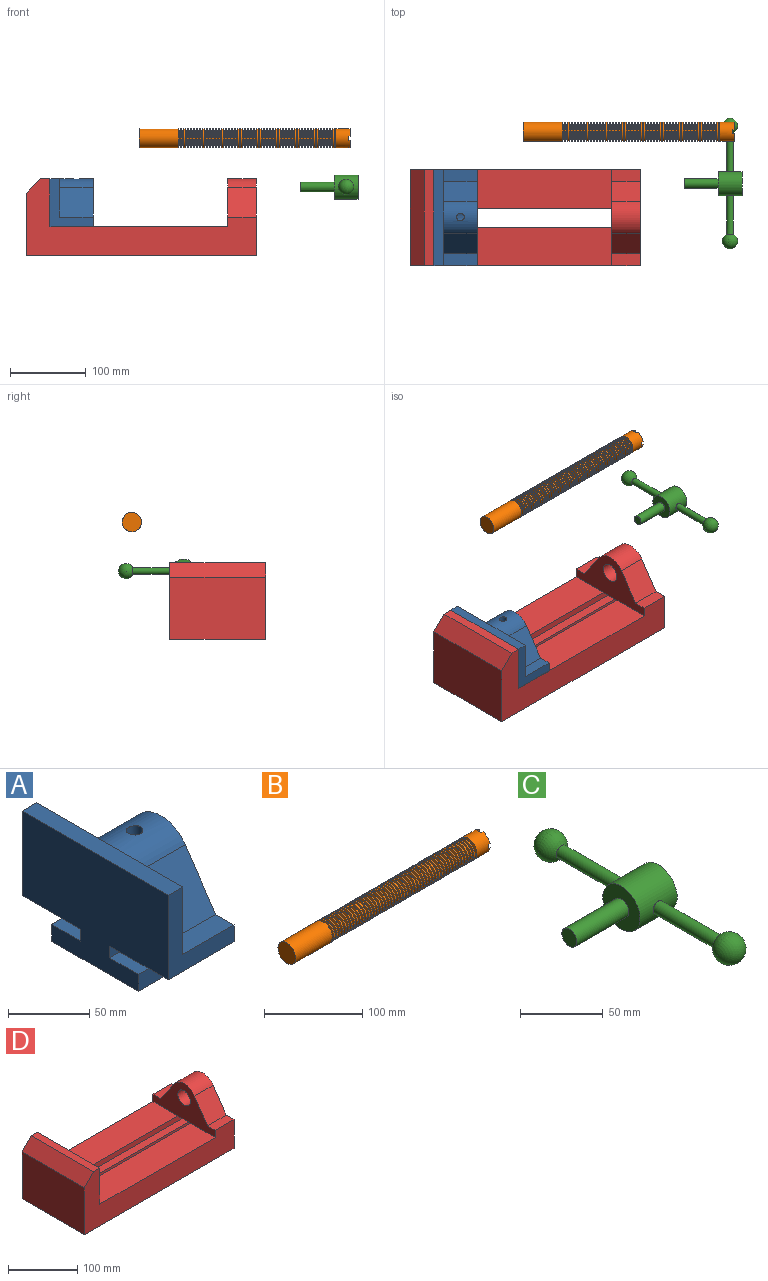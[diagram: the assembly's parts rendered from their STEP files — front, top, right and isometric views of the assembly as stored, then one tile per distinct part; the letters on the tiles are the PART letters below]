
ASSEMBLY  parts=4 mates=1
PART A: 23 faces, bbox 57.2x127x85.1 mm
  f0: plane 57.15x50.8mm, normal (0,0,-1), area 2903.2mm2, adj f3,f7,f8,f16
  f1: plane 44.45x15.91mm, normal (0,0,1), area 707.2mm2, adj f3,f5,f9,f11
  f2: plane 57.15x50.8mm, normal (0,0,-1), area 2903.2mm2, adj f3,f7,f9,f22
  f3: plane 127x84.76mm, normal (1,0,0), area 5318.8mm2, adj f0,f1,f2,f4,f8,f9,f10,f11
  f4: plane 44.45x15.84mm, normal (0,0,1), area 704mm2, adj f3,f5,f8,f10
  f5: plane 127x50.8mm, normal (1,0,0), area 3422.8mm2, adj f1,f4,f6,f8,f9,f10,f11,f13
  f6: plane 127x12.7mm, normal (0,0,1), area 1612.9mm2, adj f5,f7,f8,f9
  f7: plane 127x85.09mm, normal (-1,0,0), area 9248.3mm2, adj f0,f2,f6,f8,f9,f16,f17,f18
  f8: plane 63.5x57.15mm, normal (0,-1,0), area 1371mm2, adj f0,f3,f4,f5,f6,f7
  f9: plane 63.5x57.15mm, normal (0,1,0), area 1371mm2, adj f1,f2,f3,f5,f6,f7
  f10: plane 44.45x39.31mm, normal (0,-0.83,0.56), area 2110mm2, adj f3,f4,f5,f13
  f11: plane 44.45x39.29mm, normal (0,0.83,0.56), area 2108.2mm2, adj f1,f3,f5,f13
  f12: cylinder r=12.7mm len=44.45mm, axis (1,0,0), area 3463.8mm2, adj f3,f14,f15
  f13: cylinder r=25.4mm len=44.45mm, axis (1,0,0), area 2122.5mm2, adj f3,f5,f10,f11,f15
  f14: plane 25.4x25.4mm, normal (1,0,0), area 506.7mm2, adj f12
  f15: cylinder r=5.08mm len=13.76mm, axis (0,0,1), area 403.7mm2, adj f12,f13
  f16: plane 57.15x8.89mm, normal (0,-1,0), area 508.1mm2, adj f0,f3,f7,f17
  f17: plane 57.15x25.02mm, normal (0,0,1), area 1429.6mm2, adj f3,f7,f16,f18
  f18: plane 57.15x12.7mm, normal (0,-1,0), area 725.8mm2, adj f3,f7,f17,f19
  f19: plane 75.43x57.15mm, normal (0,0,-1), area 4310.9mm2, adj f3,f7,f18,f20
  f20: plane 57.15x12.7mm, normal (0,1,0), area 725.8mm2, adj f3,f7,f19,f21
  f21: plane 57.15x25.02mm, normal (0,0,1), area 1429.6mm2, adj f3,f7,f20,f22
  f22: plane 57.15x8.89mm, normal (0,1,0), area 508.1mm2, adj f2,f3,f7,f21
PART B: 220 faces, bbox 279.4x25.4x25.4 mm
  f0: cylinder r=12.7mm len=25.4mm, axis (-1,0,0), area 1468.2mm2, adj f1,f2,f3,f4,f7,f208,f209,f210
  f1: plane 9.9x9.9mm, normal (1,0,0), area 62.3mm2, adj f0,f5,f215,f217
  f2: plane 9.9x9.9mm, normal (1,0,0), area 62.3mm2, adj f0,f5,f209,f218
  f3: plane 9.9x9.9mm, normal (1,0,0), area 62.3mm2, adj f0,f5,f211,f214
  f4: plane 9.9x9.9mm, normal (1,0,0), area 62.3mm2, adj f0,f5,f208,f212
  f5: cylinder r=6.35mm len=25.4mm, axis (1,0,0), area 960.3mm2, adj f1,f2,f3,f4,f6,f208,f209,f210
  f6: plane 12.7x12.7mm, normal (1,0,0), area 126.7mm2, adj f5
  f7: cone r=12.7mm half-angle=76deg, axis (1,0,0), area 188mm2, adj f0,f9
  f8: cone r=12.7mm half-angle=76deg, axis (-1,0,0), area 188mm2, adj f9,f10
  f9: cylinder r=10.16mm len=20.32mm, axis (1,0,0), area 81.1mm2, adj f7,f8
  f10: cylinder r=12.7mm len=25.4mm, axis (-1,0,0), area 131.7mm2, adj f8,f11
  f11: cone r=12.7mm half-angle=76deg, axis (1,0,0), area 188mm2, adj f10,f13
  f12: cone r=12.7mm half-angle=76deg, axis (-1,0,0), area 188mm2, adj f13,f14
  f13: cylinder r=10.16mm len=20.32mm, axis (1,0,0), area 81.1mm2, adj f11,f12
  f14: cylinder r=12.7mm len=25.4mm, axis (-1,0,0), area 131.7mm2, adj f12,f15
  f15: cone r=12.7mm half-angle=76deg, axis (1,0,0), area 188mm2, adj f14,f17
  f16: cone r=12.7mm half-angle=76deg, axis (-1,0,0), area 188mm2, adj f17,f18
  f17: cylinder r=10.16mm len=20.32mm, axis (1,0,0), area 81.1mm2, adj f15,f16
  f18: cylinder r=12.7mm len=25.4mm, axis (-1,0,0), area 131.7mm2, adj f16,f19
  f19: cone r=12.7mm half-angle=76deg, axis (1,0,0), area 188mm2, adj f18,f21
  f20: cone r=12.7mm half-angle=76deg, axis (-1,0,0), area 188mm2, adj f21,f22
  f21: cylinder r=10.16mm len=20.32mm, axis (1,0,0), area 81.1mm2, adj f19,f20
  f22: cylinder r=12.7mm len=25.4mm, axis (-1,0,0), area 131.7mm2, adj f20,f23
  f23: cone r=12.7mm half-angle=76deg, axis (1,0,0), area 188mm2, adj f22,f25
  f24: cone r=12.7mm half-angle=76deg, axis (-1,0,0), area 188mm2, adj f25,f26
  f25: cylinder r=10.16mm len=20.32mm, axis (1,0,0), area 81.1mm2, adj f23,f24
  f26: cylinder r=12.7mm len=25.4mm, axis (-1,0,0), area 131.7mm2, adj f24,f27
  f27: cone r=12.7mm half-angle=76deg, axis (1,0,0), area 188mm2, adj f26,f29
  f28: cone r=12.7mm half-angle=76deg, axis (-1,0,0), area 188mm2, adj f29,f30
  f29: cylinder r=10.16mm len=20.32mm, axis (1,0,0), area 81.1mm2, adj f27,f28
  f30: cylinder r=12.7mm len=25.4mm, axis (-1,0,0), area 131.7mm2, adj f28,f31
  f31: cone r=12.7mm half-angle=76deg, axis (1,0,0), area 188mm2, adj f30,f33
  f32: cone r=12.7mm half-angle=76deg, axis (-1,0,0), area 188mm2, adj f33,f34
  f33: cylinder r=10.16mm len=20.32mm, axis (1,0,0), area 81.1mm2, adj f31,f32
  f34: cylinder r=12.7mm len=25.4mm, axis (-1,0,0), area 131.7mm2, adj f32,f35
  f35: cone r=12.7mm half-angle=76deg, axis (1,0,0), area 188mm2, adj f34,f37
  f36: cone r=12.7mm half-angle=76deg, axis (-1,0,0), area 188mm2, adj f37,f38
  f37: cylinder r=10.16mm len=20.32mm, axis (1,0,0), area 81.1mm2, adj f35,f36
  f38: cylinder r=12.7mm len=25.4mm, axis (-1,0,0), area 131.7mm2, adj f36,f39
  f39: cone r=12.7mm half-angle=76deg, axis (1,0,0), area 188mm2, adj f38,f41
  f40: cone r=12.7mm half-angle=76deg, axis (-1,0,0), area 188mm2, adj f41,f42
  f41: cylinder r=10.16mm len=20.32mm, axis (1,0,0), area 81.1mm2, adj f39,f40
  f42: cylinder r=12.7mm len=25.4mm, axis (-1,0,0), area 131.7mm2, adj f40,f43
  f43: cone r=12.7mm half-angle=76deg, axis (1,0,0), area 188mm2, adj f42,f45
  f44: cone r=12.7mm half-angle=76deg, axis (-1,0,0), area 188mm2, adj f45,f46
  f45: cylinder r=10.16mm len=20.32mm, axis (1,0,0), area 81.1mm2, adj f43,f44
  f46: cylinder r=12.7mm len=25.4mm, axis (-1,0,0), area 131.7mm2, adj f44,f47
  f47: cone r=12.7mm half-angle=76deg, axis (1,0,0), area 188mm2, adj f46,f49
  f48: cone r=12.7mm half-angle=76deg, axis (-1,0,0), area 188mm2, adj f49,f50
  f49: cylinder r=10.16mm len=20.32mm, axis (1,0,0), area 81.1mm2, adj f47,f48
  f50: cylinder r=12.7mm len=25.4mm, axis (-1,0,0), area 131.7mm2, adj f48,f51
  f51: cone r=12.7mm half-angle=76deg, axis (1,0,0), area 188mm2, adj f50,f53
  f52: cone r=12.7mm half-angle=76deg, axis (-1,0,0), area 188mm2, adj f53,f54
  f53: cylinder r=10.16mm len=20.32mm, axis (1,0,0), area 81.1mm2, adj f51,f52
  f54: cylinder r=12.7mm len=25.4mm, axis (-1,0,0), area 131.7mm2, adj f52,f55
  f55: cone r=12.7mm half-angle=76deg, axis (1,0,0), area 188mm2, adj f54,f57
  f56: cone r=12.7mm half-angle=76deg, axis (-1,0,0), area 188mm2, adj f57,f58
  f57: cylinder r=10.16mm len=20.32mm, axis (1,0,0), area 81.1mm2, adj f55,f56
  f58: cylinder r=12.7mm len=25.4mm, axis (-1,0,0), area 131.7mm2, adj f56,f59
  f59: cone r=12.7mm half-angle=76deg, axis (1,0,0), area 188mm2, adj f58,f61
  f60: cone r=12.7mm half-angle=76deg, axis (-1,0,0), area 188mm2, adj f61,f62
  f61: cylinder r=10.16mm len=20.32mm, axis (1,0,0), area 81.1mm2, adj f59,f60
  f62: cylinder r=12.7mm len=25.4mm, axis (-1,0,0), area 131.7mm2, adj f60,f63
  f63: cone r=12.7mm half-angle=76deg, axis (1,0,0), area 188mm2, adj f62,f65
  f64: cone r=12.7mm half-angle=76deg, axis (-1,0,0), area 188mm2, adj f65,f66
  f65: cylinder r=10.16mm len=20.32mm, axis (1,0,0), area 81.1mm2, adj f63,f64
  f66: cylinder r=12.7mm len=25.4mm, axis (-1,0,0), area 131.7mm2, adj f64,f67
  f67: cone r=12.7mm half-angle=76deg, axis (1,0,0), area 188mm2, adj f66,f69
  f68: cone r=12.7mm half-angle=76deg, axis (-1,0,0), area 188mm2, adj f69,f70
  f69: cylinder r=10.16mm len=20.32mm, axis (1,0,0), area 81.1mm2, adj f67,f68
  f70: cylinder r=12.7mm len=25.4mm, axis (-1,0,0), area 131.7mm2, adj f68,f71
  f71: cone r=12.7mm half-angle=76deg, axis (1,0,0), area 188mm2, adj f70,f73
  f72: cone r=12.7mm half-angle=76deg, axis (-1,0,0), area 188mm2, adj f73,f74
  f73: cylinder r=10.16mm len=20.32mm, axis (1,0,0), area 81.1mm2, adj f71,f72
  f74: cylinder r=12.7mm len=25.4mm, axis (-1,0,0), area 131.7mm2, adj f72,f75
  f75: cone r=12.7mm half-angle=76deg, axis (1,0,0), area 188mm2, adj f74,f77
  f76: cone r=12.7mm half-angle=76deg, axis (-1,0,0), area 188mm2, adj f77,f78
  f77: cylinder r=10.16mm len=20.32mm, axis (1,0,0), area 81.1mm2, adj f75,f76
  f78: cylinder r=12.7mm len=25.4mm, axis (-1,0,0), area 131.7mm2, adj f76,f79
  f79: cone r=12.7mm half-angle=76deg, axis (1,0,0), area 188mm2, adj f78,f81
  f80: cone r=12.7mm half-angle=76deg, axis (-1,0,0), area 188mm2, adj f81,f82
  f81: cylinder r=10.16mm len=20.32mm, axis (1,0,0), area 81.1mm2, adj f79,f80
  f82: cylinder r=12.7mm len=25.4mm, axis (-1,0,0), area 131.7mm2, adj f80,f83
  f83: cone r=12.7mm half-angle=76deg, axis (1,0,0), area 188mm2, adj f82,f85
  f84: cone r=12.7mm half-angle=76deg, axis (-1,0,0), area 188mm2, adj f85,f86
  f85: cylinder r=10.16mm len=20.32mm, axis (1,0,0), area 81.1mm2, adj f83,f84
  f86: cylinder r=12.7mm len=25.4mm, axis (-1,0,0), area 131.7mm2, adj f84,f87
  f87: cone r=12.7mm half-angle=76deg, axis (1,0,0), area 188mm2, adj f86,f89
  f88: cone r=12.7mm half-angle=76deg, axis (-1,0,0), area 188mm2, adj f89,f90
  f89: cylinder r=10.16mm len=20.32mm, axis (1,0,0), area 81.1mm2, adj f87,f88
  f90: cylinder r=12.7mm len=25.4mm, axis (-1,0,0), area 131.7mm2, adj f88,f91
  f91: cone r=12.7mm half-angle=76deg, axis (1,0,0), area 188mm2, adj f90,f93
  f92: cone r=12.7mm half-angle=76deg, axis (-1,0,0), area 188mm2, adj f93,f94
  f93: cylinder r=10.16mm len=20.32mm, axis (1,0,0), area 81.1mm2, adj f91,f92
  f94: cylinder r=12.7mm len=25.4mm, axis (-1,0,0), area 131.7mm2, adj f92,f95
  f95: cone r=12.7mm half-angle=76deg, axis (1,0,0), area 188mm2, adj f94,f97
  f96: cone r=12.7mm half-angle=76deg, axis (-1,0,0), area 188mm2, adj f97,f98
  f97: cylinder r=10.16mm len=20.32mm, axis (1,0,0), area 81.1mm2, adj f95,f96
  f98: cylinder r=12.7mm len=25.4mm, axis (-1,0,0), area 131.7mm2, adj f96,f99
  f99: cone r=12.7mm half-angle=76deg, axis (1,0,0), area 188mm2, adj f98,f101
  f100: cone r=12.7mm half-angle=76deg, axis (-1,0,0), area 188mm2, adj f101,f102
  f101: cylinder r=10.16mm len=20.32mm, axis (1,0,0), area 81.1mm2, adj f99,f100
  f102: cylinder r=12.7mm len=25.4mm, axis (-1,0,0), area 131.7mm2, adj f100,f103
  f103: cone r=12.7mm half-angle=76deg, axis (1,0,0), area 188mm2, adj f102,f105
  f104: cone r=12.7mm half-angle=76deg, axis (-1,0,0), area 188mm2, adj f105,f106
  f105: cylinder r=10.16mm len=20.32mm, axis (1,0,0), area 81.1mm2, adj f103,f104
  f106: cylinder r=12.7mm len=25.4mm, axis (-1,0,0), area 131.7mm2, adj f104,f107
  f107: cone r=12.7mm half-angle=76deg, axis (1,0,0), area 188mm2, adj f106,f109
  f108: cone r=12.7mm half-angle=76deg, axis (-1,0,0), area 188mm2, adj f109,f110
  f109: cylinder r=10.16mm len=20.32mm, axis (1,0,0), area 81.1mm2, adj f107,f108
  f110: cylinder r=12.7mm len=25.4mm, axis (-1,0,0), area 131.7mm2, adj f108,f111
  f111: cone r=12.7mm half-angle=76deg, axis (1,0,0), area 188mm2, adj f110,f113
  f112: cone r=12.7mm half-angle=76deg, axis (-1,0,0), area 188mm2, adj f113,f114
  f113: cylinder r=10.16mm len=20.32mm, axis (1,0,0), area 81.1mm2, adj f111,f112
  f114: cylinder r=12.7mm len=25.4mm, axis (-1,0,0), area 131.7mm2, adj f112,f115
  f115: cone r=12.7mm half-angle=76deg, axis (1,0,0), area 188mm2, adj f114,f117
  f116: cone r=12.7mm half-angle=76deg, axis (-1,0,0), area 188mm2, adj f117,f118
  f117: cylinder r=10.16mm len=20.32mm, axis (1,0,0), area 81.1mm2, adj f115,f116
  f118: cylinder r=12.7mm len=25.4mm, axis (-1,0,0), area 131.7mm2, adj f116,f119
  f119: cone r=12.7mm half-angle=76deg, axis (1,0,0), area 188mm2, adj f118,f121
  f120: cone r=12.7mm half-angle=76deg, axis (-1,0,0), area 188mm2, adj f121,f122
  f121: cylinder r=10.16mm len=20.32mm, axis (1,0,0), area 81.1mm2, adj f119,f120
  f122: cylinder r=12.7mm len=25.4mm, axis (-1,0,0), area 131.7mm2, adj f120,f123
  f123: cone r=12.7mm half-angle=76deg, axis (1,0,0), area 188mm2, adj f122,f125
  f124: cone r=12.7mm half-angle=76deg, axis (-1,0,0), area 188mm2, adj f125,f126
  f125: cylinder r=10.16mm len=20.32mm, axis (1,0,0), area 81.1mm2, adj f123,f124
  f126: cylinder r=12.7mm len=25.4mm, axis (-1,0,0), area 131.7mm2, adj f124,f127
  f127: cone r=12.7mm half-angle=76deg, axis (1,0,0), area 188mm2, adj f126,f129
  f128: cone r=12.7mm half-angle=76deg, axis (-1,0,0), area 188mm2, adj f129,f130
  f129: cylinder r=10.16mm len=20.32mm, axis (1,0,0), area 81.1mm2, adj f127,f128
  f130: cylinder r=12.7mm len=25.4mm, axis (-1,0,0), area 131.7mm2, adj f128,f131
  f131: cone r=12.7mm half-angle=76deg, axis (1,0,0), area 188mm2, adj f130,f133
  f132: cone r=12.7mm half-angle=76deg, axis (-1,0,0), area 188mm2, adj f133,f134
  f133: cylinder r=10.16mm len=20.32mm, axis (1,0,0), area 81.1mm2, adj f131,f132
  f134: cylinder r=12.7mm len=25.4mm, axis (-1,0,0), area 131.7mm2, adj f132,f135
  f135: cone r=12.7mm half-angle=76deg, axis (1,0,0), area 188mm2, adj f134,f137
  f136: cone r=12.7mm half-angle=76deg, axis (-1,0,0), area 188mm2, adj f137,f138
  f137: cylinder r=10.16mm len=20.32mm, axis (1,0,0), area 81.1mm2, adj f135,f136
  f138: cylinder r=12.7mm len=25.4mm, axis (-1,0,0), area 131.7mm2, adj f136,f139
  f139: cone r=12.7mm half-angle=76deg, axis (1,0,0), area 188mm2, adj f138,f141
  f140: cone r=12.7mm half-angle=76deg, axis (-1,0,0), area 188mm2, adj f141,f142
  f141: cylinder r=10.16mm len=20.32mm, axis (1,0,0), area 81.1mm2, adj f139,f140
  f142: cylinder r=12.7mm len=25.4mm, axis (-1,0,0), area 131.7mm2, adj f140,f143
  f143: cone r=12.7mm half-angle=76deg, axis (1,0,0), area 188mm2, adj f142,f145
  f144: cone r=12.7mm half-angle=76deg, axis (-1,0,0), area 188mm2, adj f145,f146
  f145: cylinder r=10.16mm len=20.32mm, axis (1,0,0), area 81.1mm2, adj f143,f144
  f146: cylinder r=12.7mm len=25.4mm, axis (-1,0,0), area 131.7mm2, adj f144,f147
  f147: cone r=12.7mm half-angle=76deg, axis (1,0,0), area 188mm2, adj f146,f149
  f148: cone r=12.7mm half-angle=76deg, axis (-1,0,0), area 188mm2, adj f149,f150
  f149: cylinder r=10.16mm len=20.32mm, axis (1,0,0), area 81.1mm2, adj f147,f148
  f150: cylinder r=12.7mm len=25.4mm, axis (-1,0,0), area 131.7mm2, adj f148,f151
  f151: cone r=12.7mm half-angle=76deg, axis (1,0,0), area 188mm2, adj f150,f153
  f152: cone r=12.7mm half-angle=76deg, axis (-1,0,0), area 188mm2, adj f153,f154
  f153: cylinder r=10.16mm len=20.32mm, axis (1,0,0), area 81.1mm2, adj f151,f152
  f154: cylinder r=12.7mm len=25.4mm, axis (-1,0,0), area 131.7mm2, adj f152,f155
  f155: cone r=12.7mm half-angle=76deg, axis (1,0,0), area 188mm2, adj f154,f157
  f156: cone r=12.7mm half-angle=76deg, axis (-1,0,0), area 188mm2, adj f157,f158
  f157: cylinder r=10.16mm len=20.32mm, axis (1,0,0), area 81.1mm2, adj f155,f156
  f158: cylinder r=12.7mm len=25.4mm, axis (-1,0,0), area 131.7mm2, adj f156,f159
  f159: cone r=12.7mm half-angle=76deg, axis (1,0,0), area 188mm2, adj f158,f161
  f160: cone r=12.7mm half-angle=76deg, axis (-1,0,0), area 188mm2, adj f161,f162
  f161: cylinder r=10.16mm len=20.32mm, axis (1,0,0), area 81.1mm2, adj f159,f160
  f162: cylinder r=12.7mm len=25.4mm, axis (-1,0,0), area 131.7mm2, adj f160,f163
  f163: cone r=12.7mm half-angle=76deg, axis (1,0,0), area 188mm2, adj f162,f165
  f164: cone r=12.7mm half-angle=76deg, axis (-1,0,0), area 188mm2, adj f165,f166
  f165: cylinder r=10.16mm len=20.32mm, axis (1,0,0), area 81.1mm2, adj f163,f164
  f166: cylinder r=12.7mm len=25.4mm, axis (-1,0,0), area 131.7mm2, adj f164,f167
  f167: cone r=12.7mm half-angle=76deg, axis (1,0,0), area 188mm2, adj f166,f169
  f168: cone r=12.7mm half-angle=76deg, axis (-1,0,0), area 188mm2, adj f169,f170
  f169: cylinder r=10.16mm len=20.32mm, axis (1,0,0), area 81.1mm2, adj f167,f168
  f170: cylinder r=12.7mm len=25.4mm, axis (-1,0,0), area 131.7mm2, adj f168,f171
  f171: cone r=12.7mm half-angle=76deg, axis (1,0,0), area 188mm2, adj f170,f173
  f172: cone r=12.7mm half-angle=76deg, axis (-1,0,0), area 188mm2, adj f173,f174
  f173: cylinder r=10.16mm len=20.32mm, axis (1,0,0), area 81.1mm2, adj f171,f172
  f174: cylinder r=12.7mm len=25.4mm, axis (-1,0,0), area 131.7mm2, adj f172,f175
  f175: cone r=12.7mm half-angle=76deg, axis (1,0,0), area 188mm2, adj f174,f177
  f176: cone r=12.7mm half-angle=76deg, axis (-1,0,0), area 188mm2, adj f177,f178
  f177: cylinder r=10.16mm len=20.32mm, axis (1,0,0), area 81.1mm2, adj f175,f176
  f178: cylinder r=12.7mm len=25.4mm, axis (-1,0,0), area 131.7mm2, adj f176,f179
  f179: cone r=12.7mm half-angle=76deg, axis (1,0,0), area 188mm2, adj f178,f181
  f180: cone r=12.7mm half-angle=76deg, axis (-1,0,0), area 188mm2, adj f181,f182
  f181: cylinder r=10.16mm len=20.32mm, axis (1,0,0), area 81.1mm2, adj f179,f180
  f182: cylinder r=12.7mm len=25.4mm, axis (-1,0,0), area 131.7mm2, adj f180,f183
  f183: cone r=12.7mm half-angle=76deg, axis (1,0,0), area 188mm2, adj f182,f185
  f184: cone r=12.7mm half-angle=76deg, axis (-1,0,0), area 188mm2, adj f185,f186
  f185: cylinder r=10.16mm len=20.32mm, axis (1,0,0), area 81.1mm2, adj f183,f184
  f186: cylinder r=12.7mm len=25.4mm, axis (-1,0,0), area 131.7mm2, adj f184,f187
  f187: cone r=12.7mm half-angle=76deg, axis (1,0,0), area 188mm2, adj f186,f189
  f188: cone r=12.7mm half-angle=76deg, axis (-1,0,0), area 188mm2, adj f189,f190
  f189: cylinder r=10.16mm len=20.32mm, axis (1,0,0), area 81.1mm2, adj f187,f188
  f190: cylinder r=12.7mm len=25.4mm, axis (-1,0,0), area 131.7mm2, adj f188,f191
  f191: cone r=12.7mm half-angle=76deg, axis (1,0,0), area 188mm2, adj f190,f193
  f192: cone r=12.7mm half-angle=76deg, axis (-1,0,0), area 188mm2, adj f193,f194
  f193: cylinder r=10.16mm len=20.32mm, axis (1,0,0), area 81.1mm2, adj f191,f192
  f194: cylinder r=12.7mm len=25.4mm, axis (-1,0,0), area 131.7mm2, adj f192,f195
  f195: cone r=12.7mm half-angle=76deg, axis (1,0,0), area 188mm2, adj f194,f197
  f196: cone r=12.7mm half-angle=76deg, axis (-1,0,0), area 188mm2, adj f197,f198
  f197: cylinder r=10.16mm len=20.32mm, axis (1,0,0), area 81.1mm2, adj f195,f196
  f198: cylinder r=12.7mm len=25.4mm, axis (-1,0,0), area 131.7mm2, adj f196,f199
  f199: cone r=12.7mm half-angle=76deg, axis (1,0,0), area 188mm2, adj f198,f201
  f200: cone r=12.7mm half-angle=76deg, axis (-1,0,0), area 188mm2, adj f201,f202
  f201: cylinder r=10.16mm len=20.32mm, axis (1,0,0), area 81.1mm2, adj f199,f200
  f202: cylinder r=12.7mm len=25.4mm, axis (-1,0,0), area 131.7mm2, adj f200,f203
  f203: cone r=12.7mm half-angle=76deg, axis (1,0,0), area 188mm2, adj f202,f205
  f204: cone r=12.7mm half-angle=76deg, axis (-1,0,0), area 188mm2, adj f205,f207
  f205: cylinder r=10.16mm len=20.32mm, axis (1,0,0), area 81.1mm2, adj f203,f204
  f206: plane 25.4x25.4mm, normal (-1,0,0), area 506.7mm2, adj f207
  f207: cylinder r=12.7mm len=52.45mm, axis (-1,0,0), area 4185.4mm2, adj f204,f206
  f208: plane 6.62x2.54mm, normal (0,0,1), area 16.8mm2, adj f0,f4,f5,f210
  f209: plane 6.62x2.54mm, normal (0,0,-1), area 16.8mm2, adj f0,f2,f5,f210
  f210: plane 6.88x5.08mm, normal (1,0,0), area 32.7mm2, adj f0,f5,f208,f209
  f211: plane 6.62x2.54mm, normal (0,-1,0), area 16.8mm2, adj f0,f3,f5,f213
  f212: plane 6.62x2.54mm, normal (0,1,0), area 16.8mm2, adj f0,f4,f5,f213
  f213: plane 6.88x5.08mm, normal (1,0,0), area 32.7mm2, adj f0,f5,f211,f212
  f214: plane 6.62x2.54mm, normal (0,0,1), area 16.8mm2, adj f0,f3,f5,f216
  f215: plane 6.62x2.54mm, normal (0,0,-1), area 16.8mm2, adj f0,f1,f5,f216
  f216: plane 6.88x5.08mm, normal (1,0,0), area 32.7mm2, adj f0,f5,f214,f215
  f217: plane 6.62x2.54mm, normal (0,-1,0), area 16.8mm2, adj f0,f1,f5,f219
  f218: plane 6.62x2.54mm, normal (0,1,0), area 16.8mm2, adj f0,f2,f5,f219
  f219: plane 6.88x5.08mm, normal (1,0,0), area 32.7mm2, adj f0,f5,f217,f218
PART C: 13 faces, bbox 76.2x172.7x31.8 mm
  f0: cylinder r=4.45mm len=51.82mm, axis (0,1,0), area 1438.5mm2, adj f1,f8
  f1: cylinder r=15.88mm len=31.75mm, axis (-1,0,0), area 3041.6mm2, adj f0,f4,f5,f6
  f2: cylinder r=6.35mm len=44.45mm, axis (-1,0,0), area 1773.5mm2, adj f3,f5
  f3: plane 12.7x12.7mm, normal (-1,0,0), area 126.7mm2, adj f2
  f4: plane 31.75x31.75mm, normal (1,0,0), area 791.7mm2, adj f1
  f5: plane 31.75x31.75mm, normal (-1,0,0), area 665.1mm2, adj f1,f2
  f6: cylinder r=4.45mm len=51.82mm, axis (0,1,0), area 1438.5mm2, adj f1,f7
  f7: sphere r=10.16mm, area 1231.8mm2, adj f6
  f8: sphere r=10.16mm, area 1231.8mm2, adj f0
  f9: sphere r=4.45mm, area 124.1mm2, adj f10
  f10: plane 8.89x8.89mm, normal (0,-1,0), area 62.1mm2, adj f9
  f11: sphere r=4.45mm, area 124.1mm2, adj f12
  f12: plane 8.89x8.89mm, normal (0,1,0), area 62.1mm2, adj f11
PART D: 28 faces, bbox 304.8x127x101.6 mm
  f0: plane 234.95x50.8mm, normal (0,0,1), area 11935.5mm2, adj f5,f9,f16,f22
  f1: plane 234.95x50.8mm, normal (0,0,1), area 11935.5mm2, adj f5,f8,f16,f23
  f2: plane 127x82.55mm, normal (-1,0,0), area 10483.8mm2, adj f3,f7,f8,f9
  f3: plane 304.8x127mm, normal (0,0,-1), area 31774.1mm2, adj f2,f4,f5,f8,f9,f18,f27
  f4: plane 127x101.27mm, normal (1,0,0), area 7370.6mm2, adj f3,f8,f9,f10,f11,f12,f13,f14
  f5: plane 127x101.6mm, normal (1,0,0), area 9667.6mm2, adj f0,f1,f3,f6,f8,f9,f18,f19
  f6: plane 127x12.7mm, normal (0,0,1), area 1612.9mm2, adj f5,f7,f8,f9
  f7: plane 127x19.05mm, normal (-0.71,0,0.71), area 3421.5mm2, adj f2,f6,f8,f9
  f8: plane 304.8x101.6mm, normal (0,-1,0), area 13931.4mm2, adj f1,f2,f3,f4,f5,f6,f7,f14
  f9: plane 304.8x101.6mm, normal (0,1,0), area 13931.4mm2, adj f0,f2,f3,f4,f5,f6,f7,f10
  f10: plane 38.1x15.91mm, normal (0,0,1), area 606.2mm2, adj f4,f9,f11,f16
  f11: plane 39.29x38.1mm, normal (0,0.83,0.56), area 1807mm2, adj f4,f10,f12,f16
  f12: cylinder r=25.4mm len=42.08mm, axis (1,0,0), area 1889.1mm2, adj f4,f11,f13,f16
  f13: plane 39.31x38.1mm, normal (0,-0.83,0.56), area 1808.6mm2, adj f4,f12,f14,f16
  f14: plane 38.1x15.84mm, normal (0,0,1), area 603.5mm2, adj f4,f8,f13,f16
  f15: cylinder r=12.7mm len=38.1mm, axis (1,0,0), area 3040.2mm2, adj f4,f16
  f16: plane 127x63.17mm, normal (-1,0,0), area 4135mm2, adj f0,f1,f8,f9,f10,f11,f12,f13
  f17: plane 38.1x25.4mm, normal (0,0,-1), area 967.7mm2, adj f4,f16,f22,f23
  f18: plane 273.05x16.51mm, normal (0,-1,0), area 4508.1mm2, adj f3,f4,f5,f19
  f19: plane 273.05x25.02mm, normal (0,0,1), area 6830.5mm2, adj f4,f5,f18,f20
  f20: plane 273.05x12.7mm, normal (0,-1,0), area 3467.7mm2, adj f4,f5,f19,f21
  f21: plane 273.05x25.02mm, normal (0,0,-1), area 6830.5mm2, adj f4,f5,f20,f22
  f22: plane 273.05x8.89mm, normal (0,-1,0), area 2427.4mm2, adj f0,f4,f5,f17,f21
  f23: plane 273.05x8.89mm, normal (0,1,0), area 2427.4mm2, adj f1,f4,f5,f17,f24
  f24: plane 273.05x25.02mm, normal (0,0,-1), area 6830.5mm2, adj f4,f5,f23,f25
  f25: plane 273.05x12.7mm, normal (0,1,0), area 3467.7mm2, adj f4,f5,f24,f26
  f26: plane 273.05x25.02mm, normal (0,0,1), area 6830.5mm2, adj f4,f5,f25,f27
  f27: plane 273.05x16.51mm, normal (0,1,0), area 4508.1mm2, adj f3,f4,f5,f26
PLACE A rot(axis=(0,0,-1),0deg) t=(0,0,0)mm
PLACE B t=(105.29,113.48,79.03)mm
PLACE C t=(61.44,45.02,14.33)mm
PLACE D at identity fixed
MATE slider A.f7 <-> D.f5  axis (1,0,0) through (-273.05,-63.5,38.1)mm
